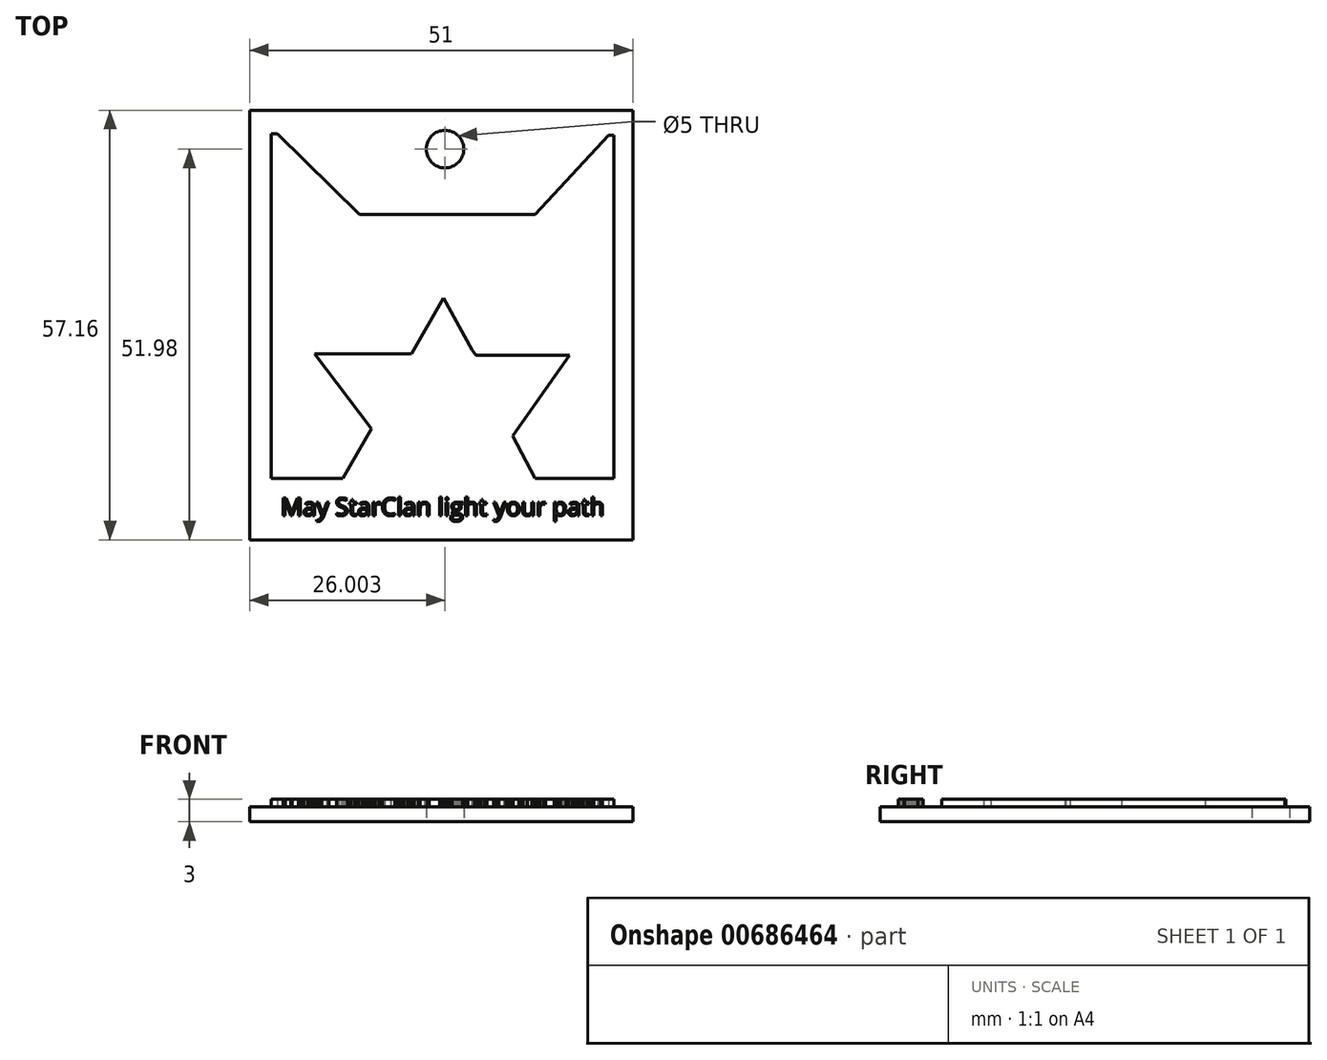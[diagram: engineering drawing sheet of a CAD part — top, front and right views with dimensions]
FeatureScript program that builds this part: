
annotation { "Feature Type Name" : "Feature", "Feature Type Description" : "" }
export const myFeature = defineFeature(function(context is Context, id is Id, definition is map)
    precondition{}
    {
        {
            var Q0;
            Q0=qCreatedBy(makeId("Top.planeOp"),FACE);
            var sketch = newSketch(context, id + "F0", { "sketchPlane" : qUnion([Q0])});
            skLineSegment(sketch, "E0", {"start": v(2.03, -1.78) * mm, "end": v(2.03, -47.58) * mm});
            skLineSegment(sketch, "E1", {"start": v(2.03, -47.58) * mm, "end": v(11.59, -47.58) * mm});
            skLineSegment(sketch, "E2", {"start": v(11.59, -47.58) * mm, "end": v(15.4, -41.03) * mm});
            skLineSegment(sketch, "E3", {"start": v(15.4, -41.03) * mm, "end": v(7.83, -31.06) * mm});
            skLineSegment(sketch, "E4", {"start": v(7.83, -31.06) * mm, "end": v(20.73, -31.06) * mm});
            skLineSegment(sketch, "E5", {"start": v(20.73, -31.06) * mm, "end": v(24.96, -23.62) * mm});
            skLineSegment(sketch, "E6", {"start": v(24.96, -23.62) * mm, "end": v(28.78, -30.52) * mm});
            skLineSegment(sketch, "E7", {"start": v(28.78, -30.52) * mm, "end": v(29.26, -31.2) * mm});
            skLineSegment(sketch, "E8", {"start": v(29.26, -31.2) * mm, "end": v(41.75, -31.2) * mm});
            skLineSegment(sketch, "E9", {"start": v(41.75, -31.2) * mm, "end": v(34.17, -41.98) * mm});
            skLineSegment(sketch, "E10", {"start": v(34.17, -41.98) * mm, "end": v(37.18, -47.58) * mm});
            skLineSegment(sketch, "E11", {"start": v(37.18, -47.58) * mm, "end": v(47.62, -47.58) * mm});
            skLineSegment(sketch, "E12", {"start": v(47.62, -47.58) * mm, "end": v(47.62, -1.92) * mm});
            skLineSegment(sketch, "E13", {"start": v(47.62, -1.92) * mm, "end": v(46.94, -1.92) * mm});
            skLineSegment(sketch, "E14", {"start": v(46.94, -1.92) * mm, "end": v(37.18, -12.5) * mm});
            skLineSegment(sketch, "E15", {"start": v(37.18, -12.5) * mm, "end": v(13.77, -12.5) * mm});
            skLineSegment(sketch, "E16", {"start": v(13.77, -12.5) * mm, "end": v(2.85, -1.78) * mm});
            skLineSegment(sketch, "E17", {"start": v(2.85, -1.78) * mm, "end": v(2.03, -1.78) * mm});
            skSolve(sketch);
        }
        {
            var Q0;
            Q0=makeQuery(id+"F0.imprint","IMPRINT",FACE,{"disambiguationData":[TD([[makeQuery(id+"F0.imprint","IMPRINT",EDGE,{"derivedFrom":sQuery(id+"F0.wireOp",EDGE,"E0")}),1.0]])]});
            extrude(context, id + "F1", {"entities" : qUnion([Q0]), "depth" : 3 * mm, "offsetDistance" : 25 * mm});
        }
        {
            var Q0;
            Q0=qCreatedBy(makeId("Top.planeOp"),FACE);
            var sketch = newSketch(context, id + "F2", { "sketchPlane" : qUnion([Q0])});
            skLineSegment(sketch, "E18.bottom", {"start": v(-0.83, 1.38) * mm, "end": v(50.17, 1.38) * mm});
            skLineSegment(sketch, "E18.top", {"start": v(-0.83, -55.78) * mm, "end": v(50.17, -55.78) * mm});
            skLineSegment(sketch, "E18.left", {"start": v(-0.83, 1.38) * mm, "end": v(-0.83, -55.78) * mm});
            skLineSegment(sketch, "E18.right", {"start": v(50.17, 1.38) * mm, "end": v(50.17, -55.78) * mm});
            skSolve(sketch);
        }
        {
            var Q0;
            Q0=makeQuery(id+"F2.imprint","IMPRINT",FACE,{"disambiguationData":[TD([[makeQuery(id+"F2.imprint","IMPRINT",EDGE,{"derivedFrom":sQuery(id+"F2.wireOp",EDGE,"E18.bottom")}),-1.0]])]});
            extrude(context, id + "F3", {"entities" : qUnion([Q0]), "operationType" : NewBodyOperationType.ADD, "depth" : 2 * mm, "offsetDistance" : 25 * mm});
        }
        {
            var Q0;
            Q0=qCreatedBy(makeId("Top.planeOp"),FACE);
            var sketch = newSketch(context, id + "F4", { "sketchPlane" : qUnion([Q0])});
            skCircle(sketch, "E19", {"center": v(25.17, -3.8) * mm, "radius": 2.06 * mm});
            skCircle(sketch, "E20", {"center": v(25.17, -3.8) * mm, "radius": 3 * mm});
            skSolve(sketch);
        }
        {
            var Q0;
            Q0=sQuery(id+"F4.wireOp",VERTEX,"E19.center");
            var Q1;
            Q1=makeQuery(id+"F1.opExtrude","SWEPT_BODY",BODY,{"disambiguationData":[OSD([sQuery(id+"F0.wireOp",EDGE,"E0"),sQuery(id+"F0.wireOp",EDGE,"E1"),sQuery(id+"F0.wireOp",EDGE,"E2"),sQuery(id+"F0.wireOp",EDGE,"E3"),sQuery(id+"F0.wireOp",EDGE,"E4"),sQuery(id+"F0.wireOp",EDGE,"E5"),sQuery(id+"F0.wireOp",EDGE,"E6"),sQuery(id+"F0.wireOp",EDGE,"E7"),sQuery(id+"F0.wireOp",EDGE,"E8"),sQuery(id+"F0.wireOp",EDGE,"E9"),sQuery(id+"F0.wireOp",EDGE,"E10"),sQuery(id+"F0.wireOp",EDGE,"E11"),sQuery(id+"F0.wireOp",EDGE,"E12"),sQuery(id+"F0.wireOp",EDGE,"E13"),sQuery(id+"F0.wireOp",EDGE,"E14"),sQuery(id+"F0.wireOp",EDGE,"E15"),sQuery(id+"F0.wireOp",EDGE,"E16"),sQuery(id+"F0.wireOp",EDGE,"E17")])]});
            hole(context, id + "F5", {"style" : HoleStyle.SIMPLE, "endStyle" : HoleEndStyle.THROUGH, "oppositeDirection" : true, "holeDiameter" : 5 * mm, "majorDiameter" : 5 * mm, "isTappedThrough" : true, "tappedDepth" : 12 * mm, "tapClearance" : 3, "locations" : qUnion([Q0]), "scope" : qUnion([Q1])});
        }
        {
            var Q0;
            Q0=makeQuery(id+"F3.opExtrude","CAP_FACE",FACE,{"disambiguationData":[OSD([sQuery(id+"F2.wireOp",EDGE,"E18.bottom"),sQuery(id+"F2.wireOp",EDGE,"E18.top"),sQuery(id+"F2.wireOp",EDGE,"E18.left"),sQuery(id+"F2.wireOp",EDGE,"E18.right")])],"isStart":false});
            var sketch = newSketch(context, id + "F6", { "sketchPlane" : qUnion([Q0])});
            skText(sketch, "E21", { "text": "May StarClan light your path", "fontName": "OpenSans-Regular.ttf"});
            const initialGuessF6  = {"E21": [0.0033, -0.05255, 1, 0, 0.00235]};
            skSetInitialGuess(sketch, initialGuessF6);
            skSolve(sketch);
        }
        {
            var Q0;
            Q0 = qSketchRegion(id + "F6", true);
            extrude(context, id + "F7", {"entities" : qUnion([Q0]), "operationType" : NewBodyOperationType.ADD, "depth" : 1 * mm, "offsetDistance" : 25 * mm});
        }
    });
